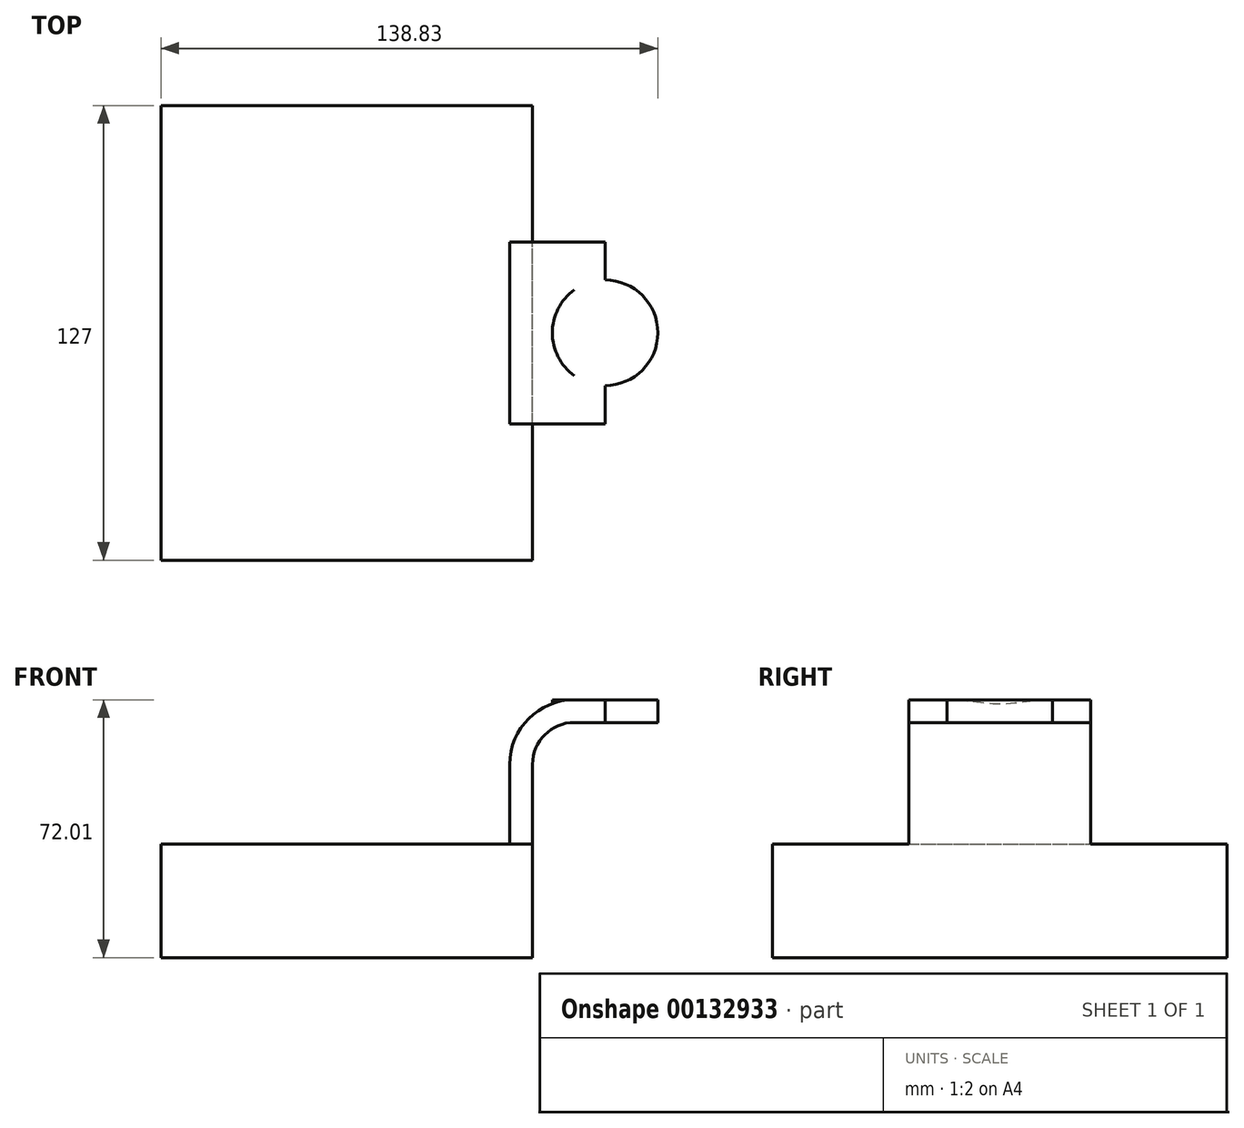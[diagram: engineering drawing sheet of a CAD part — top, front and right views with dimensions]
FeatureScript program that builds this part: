
annotation { "Feature Type Name" : "Feature", "Feature Type Description" : "" }
export const myFeature = defineFeature(function(context is Context, id is Id, definition is map)
    precondition{}
    {
        {
            var Q0;
            Q0=qCreatedBy(makeId("Front.planeOp"),FACE);
            var sketch = newSketch(context, id + "F0", { "sketchPlane" : qUnion([Q0])});
            skLineSegment(sketch, "E0.bottom", {"start": v(51.9, -15.82) * mm, "end": v(-51.9, -15.82) * mm});
            skLineSegment(sketch, "E0.top", {"start": v(51.9, 15.82) * mm, "end": v(-51.9, 15.82) * mm});
            skLineSegment(sketch, "E0.left", {"start": v(51.9, -15.82) * mm, "end": v(51.9, 15.82) * mm});
            skLineSegment(sketch, "E0.right", {"start": v(-51.9, -15.82) * mm, "end": v(-51.9, 15.82) * mm});
            skPoint(sketch, "E0.middle", {"position": v(0, 0) * mm});
            skLineSegment(sketch, "E1.bottom", {"start": v(101.67, 49.84) * mm, "end": v(72.18, 49.84) * mm});
            skLineSegment(sketch, "E1.top", {"start": v(101.67, 75.64) * mm, "end": v(72.18, 75.64) * mm});
            skLineSegment(sketch, "E1.left", {"start": v(101.67, 49.84) * mm, "end": v(101.67, 75.64) * mm});
            skLineSegment(sketch, "E1.right", {"start": v(72.18, 49.84) * mm, "end": v(72.18, 75.64) * mm});
            skPoint(sketch, "E1.middle", {"position": v(86.92, 62.74) * mm});
            skLineSegment(sketch, "E2", {"start": v(51.9, 15.82) * mm, "end": v(51.9, 38.17) * mm});
            skArc(sketch, "E3", {"start": v(51.9, 38.17) * mm, "mid": v(55.33, 46.42) * mm, "end": v(63.58, 49.84) * mm});
            skLineSegment(sketch, "E4", {"start": v(63.58, 49.84) * mm, "end": v(86.92, 49.84) * mm});
            skLineSegment(sketch, "E5.0", {"start": v(63.58, 56.19) * mm, "end": v(86.92, 56.19) * mm});
            skArc(sketch, "E5.1", {"start": v(45.56, 38.17) * mm, "mid": v(50.84, 50.9) * mm, "end": v(63.58, 56.19) * mm});
            skLineSegment(sketch, "E5.2", {"start": v(45.56, 15.82) * mm, "end": v(45.56, 38.17) * mm});
            skLineSegment(sketch, "E6", {"start": v(86.92, 49.84) * mm, "end": v(86.92, 56.19) * mm});
            skFitSpline(sketch, "E7", {"points": [v(-51.9, 15.82) * mm, v(0, 42.2) * mm, v(63.58, 56.19) * mm], "startDerivative": vector(86.89, 130.22) * mm, "endDerivative": vector(205.13, -0.1) * mm});
            skSolve(sketch);
        }
        {
            var Q0;
            {var subQ1=sQuery(id+"F0.wireOp",EDGE,"E2");Q0=makeQuery(id+"F0.imprint","IMPRINT",FACE,{"disambiguationData":[TD([[makeQuery(id+"F0.imprint","IMPRINT",EDGE,{"derivedFrom":subQ1}),1.0]])]});}
            var Q1;
            Q1=makeQuery(id+"F0.imprint","IMPRINT",FACE,{"disambiguationData":[TD([[makeQuery(id+"F0.imprint","IMPRINT",EDGE,{"derivedFrom":sQuery(id+"F0.wireOp",EDGE,"E5.1")}),1.0]])]});
            extrude(context, id + "F1", {"entities" : qUnion([Q0, Q1]), "endBound" : BoundingType.SYMMETRIC, "depth" : 50.8 * mm});
        }
        {
            var Q0;
            Q0=makeQuery(id+"F0.imprint","IMPRINT",FACE,{"disambiguationData":[TD([[makeQuery(id+"F0.imprint","IMPRINT",EDGE,{"derivedFrom":sQuery(id+"F0.wireOp",EDGE,"E0.bottom")}),-1.0]])]});
            extrude(context, id + "F2", {"entities" : qUnion([Q0]), "operationType" : NewBodyOperationType.ADD, "endBound" : BoundingType.SYMMETRIC, "depth" : 127 * mm});
        }
        {
            var Q0;
            Q0=makeQuery(id+"F0.imprint","IMPRINT",FACE,{"disambiguationData":[TD([[makeQuery(id+"F0.imprint","IMPRINT",EDGE,{"derivedFrom":sQuery(id+"F0.wireOp",EDGE,"E1.bottom")}),-1.0]])]});
            var Q1;
            Q1=sQuery(id+"F0.wireOp",EDGE,"E1.right");
            revolve(context, id + "F3", {"operationType" : NewBodyOperationType.ADD, "entities" : qUnion([Q0]), "axis" : qUnion([Q1]), "revolveType" : RevolveType.FULL});
        }
    });
